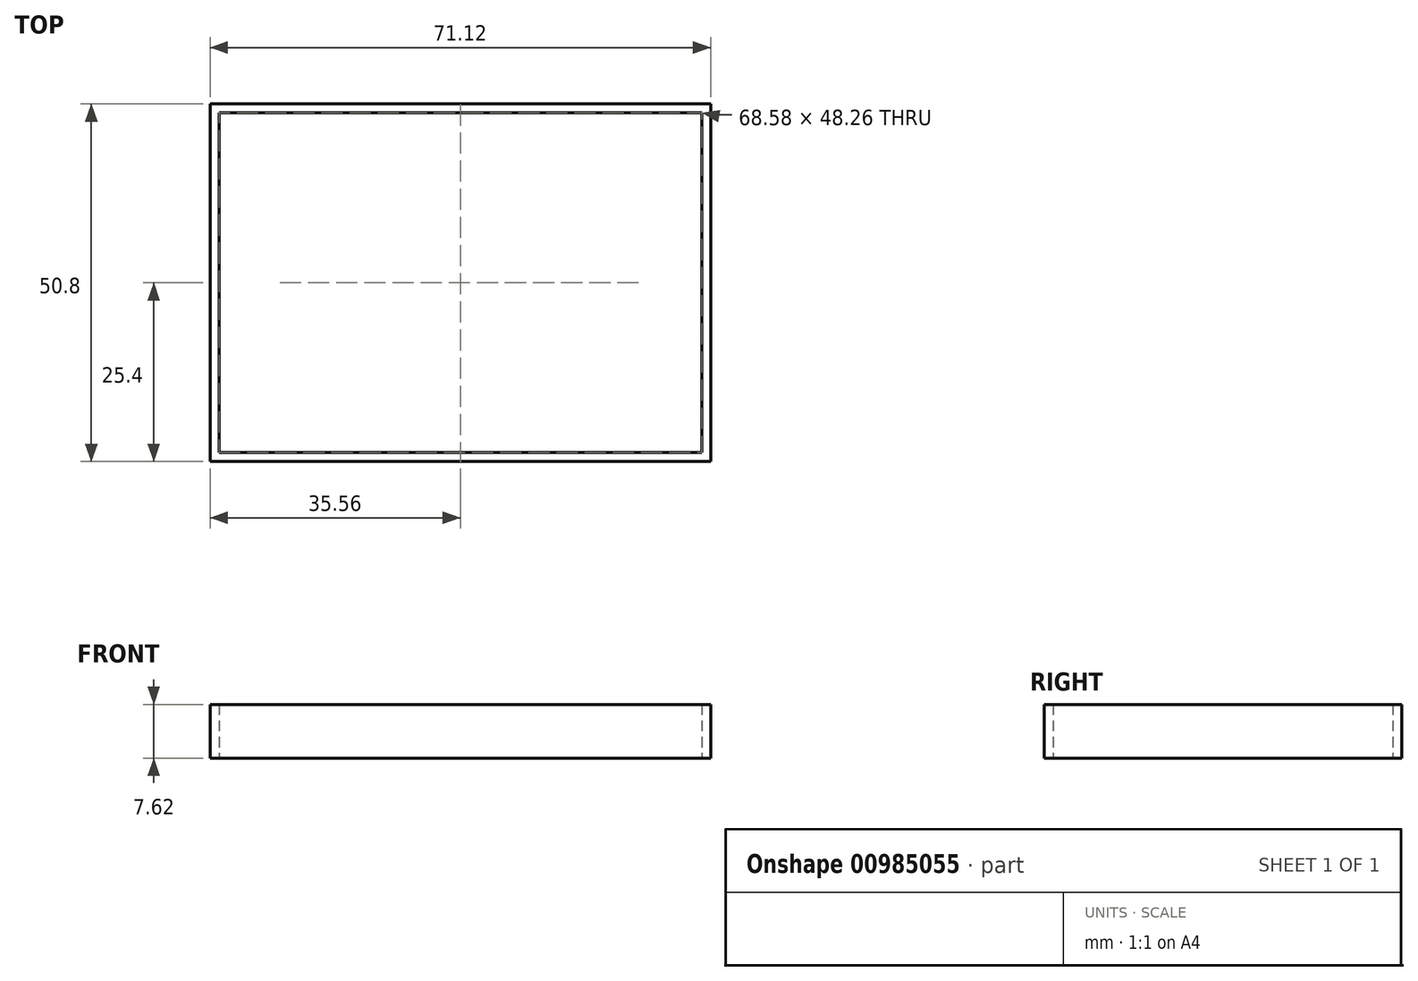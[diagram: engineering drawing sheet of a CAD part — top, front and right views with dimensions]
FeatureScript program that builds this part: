
annotation { "Feature Type Name" : "Feature", "Feature Type Description" : "" }
export const myFeature = defineFeature(function(context is Context, id is Id, definition is map)
    precondition{}
    {
        {
            var Q0;
            Q0=qCreatedBy(makeId("Top.planeOp"),FACE);
            var sketch = newSketch(context, id + "F0", { "sketchPlane" : qUnion([Q0])});
            skLineSegment(sketch, "E0.bottom", {"start": v(35.56, -25.4) * mm, "end": v(-35.56, -25.4) * mm});
            skLineSegment(sketch, "E0.top", {"start": v(35.56, 25.4) * mm, "end": v(-35.56, 25.4) * mm});
            skLineSegment(sketch, "E0.left", {"start": v(35.56, -25.4) * mm, "end": v(35.56, 25.4) * mm});
            skLineSegment(sketch, "E0.right", {"start": v(-35.56, -25.4) * mm, "end": v(-35.56, 25.4) * mm});
            skPoint(sketch, "E0.middle", {"position": v(0, 0) * mm});
            skLineSegment(sketch, "E1.bottom", {"start": v(34.3, -24.13) * mm, "end": v(-34.3, -24.13) * mm});
            skLineSegment(sketch, "E1.top", {"start": v(34.3, 24.13) * mm, "end": v(-34.3, 24.13) * mm});
            skLineSegment(sketch, "E1.left", {"start": v(34.3, -24.13) * mm, "end": v(34.3, 24.13) * mm});
            skLineSegment(sketch, "E1.right", {"start": v(-34.3, -24.13) * mm, "end": v(-34.3, 24.13) * mm});
            skSolve(sketch);
        }
        {
            var Q0;
            Q0=makeQuery(id+"F0.imprint","IMPRINT",FACE,{"disambiguationData":[TD([[makeQuery(id+"F0.imprint","IMPRINT",EDGE,{"derivedFrom":sQuery(id+"F0.wireOp",EDGE,"E0.bottom")}),-1.0]])]});
            extrude(context, id + "F1", {"entities" : qUnion([Q0]), "depth" : 7.62 * mm, "offsetDistance" : 25.4 * mm});
        }
    });
